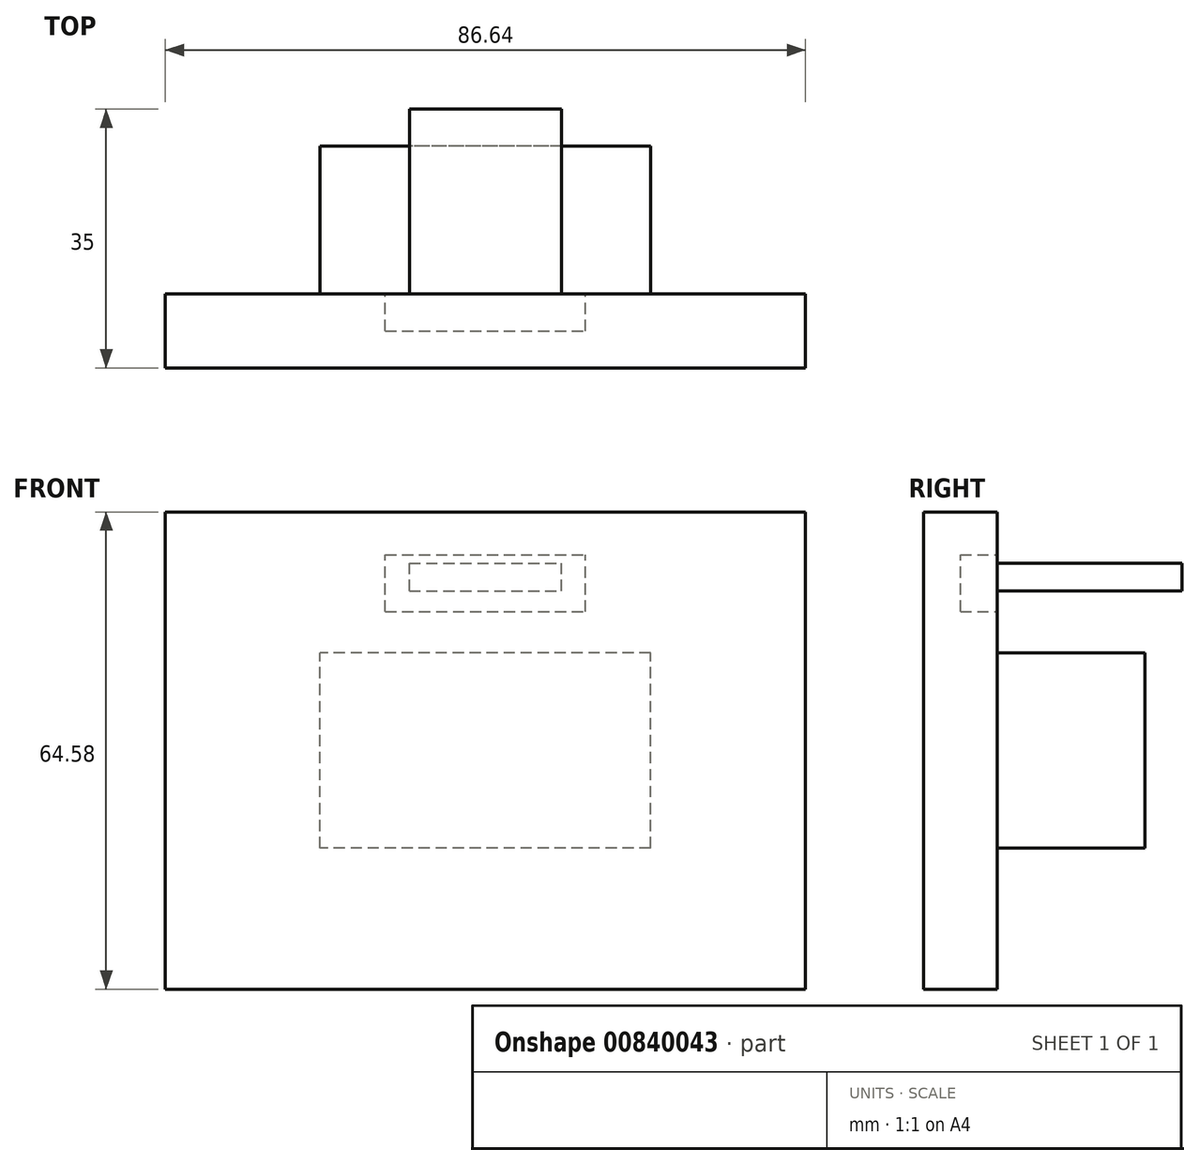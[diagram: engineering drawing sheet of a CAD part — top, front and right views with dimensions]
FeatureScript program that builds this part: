
annotation { "Feature Type Name" : "Feature", "Feature Type Description" : "" }
export const myFeature = defineFeature(function(context is Context, id is Id, definition is map)
    precondition{}
    {
        {
            var Q0;
            Q0=qCreatedBy(makeId("Front.planeOp"),FACE);
            var sketch = newSketch(context, id + "F0", { "sketchPlane" : qUnion([Q0])});
            skLineSegment(sketch, "E0.bottom", {"start": v(43.32, -32.3) * mm, "end": v(-43.32, -32.3) * mm});
            skLineSegment(sketch, "E0.top", {"start": v(43.32, 32.3) * mm, "end": v(-43.32, 32.3) * mm});
            skLineSegment(sketch, "E0.left", {"start": v(43.32, -32.3) * mm, "end": v(43.32, 32.3) * mm});
            skLineSegment(sketch, "E0.right", {"start": v(-43.32, -32.3) * mm, "end": v(-43.32, 32.3) * mm});
            skPoint(sketch, "E0.middle", {"position": v(0, 0) * mm});
            skSolve(sketch);
        }
        {
            var Q0;
            Q0 = qSketchRegion(id + "F0", true);
            extrude(context, id + "F1", {"entities" : qUnion([Q0]), "depth" : 10 * mm, "offsetDistance" : 25 * mm});
        }
        {
            var Q0;
            Q0=makeQuery(id+"F1.opExtrude","CAP_FACE",FACE,{"disambiguationData":[OSD([sQuery(id+"F0.wireOp",EDGE,"E0.bottom"),sQuery(id+"F0.wireOp",EDGE,"E0.top"),sQuery(id+"F0.wireOp",EDGE,"E0.left"),sQuery(id+"F0.wireOp",EDGE,"E0.right")])],"isStart":true});
            var sketch = newSketch(context, id + "F2", { "sketchPlane" : qUnion([Q0])});
            skLineSegment(sketch, "E1.bottom", {"start": v(13.57, 18.8) * mm, "end": v(-13.57, 18.8) * mm});
            skLineSegment(sketch, "E1.top", {"start": v(13.57, 26.46) * mm, "end": v(-13.57, 26.46) * mm});
            skLineSegment(sketch, "E1.left", {"start": v(13.57, 18.8) * mm, "end": v(13.57, 26.46) * mm});
            skLineSegment(sketch, "E1.right", {"start": v(-13.57, 18.8) * mm, "end": v(-13.57, 26.46) * mm});
            skPoint(sketch, "E1.middle", {"position": v(0, 22.63) * mm});
            skSolve(sketch);
        }
        {
            var Q0;
            Q0 = qSketchRegion(id + "F2", true);
            extrude(context, id + "F3", {"entities" : qUnion([Q0]), "operationType" : NewBodyOperationType.REMOVE, "oppositeDirection" : true, "depth" : 5 * mm, "offsetDistance" : 25 * mm});
        }
        {
            var Q0;
            Q0=makeQuery(id+"F1.opExtrude","CAP_FACE",FACE,{"disambiguationData":[OSD([sQuery(id+"F0.wireOp",EDGE,"E0.bottom"),sQuery(id+"F0.wireOp",EDGE,"E0.top"),sQuery(id+"F0.wireOp",EDGE,"E0.left"),sQuery(id+"F0.wireOp",EDGE,"E0.right")])],"isStart":true});
            var sketch = newSketch(context, id + "F4", { "sketchPlane" : qUnion([Q0])});
            skLineSegment(sketch, "E2.bottom", {"start": v(-22.37, -13.2) * mm, "end": v(22.37, -13.2) * mm});
            skLineSegment(sketch, "E2.top", {"start": v(-22.37, 13.2) * mm, "end": v(22.37, 13.2) * mm});
            skLineSegment(sketch, "E2.left", {"start": v(-22.37, -13.2) * mm, "end": v(-22.37, 13.2) * mm});
            skLineSegment(sketch, "E2.right", {"start": v(22.37, -13.2) * mm, "end": v(22.37, 13.2) * mm});
            skPoint(sketch, "E2.middle", {"position": v(0, 0) * mm});
            skSolve(sketch);
        }
        {
            var Q0;
            Q0 = qSketchRegion(id + "F4", true);
            extrude(context, id + "F5", {"entities" : qUnion([Q0]), "operationType" : NewBodyOperationType.ADD, "depth" : 20 * mm, "offsetDistance" : 25 * mm});
        }
        {
            var Q0;
            Q0=makeQuery(id+"F1.opExtrude","CAP_FACE",FACE,{"disambiguationData":[OSD([sQuery(id+"F0.wireOp",EDGE,"E0.bottom"),sQuery(id+"F0.wireOp",EDGE,"E0.top"),sQuery(id+"F0.wireOp",EDGE,"E0.left"),sQuery(id+"F0.wireOp",EDGE,"E0.right")])],"isStart":true});
            var sketch = newSketch(context, id + "F6", { "sketchPlane" : qUnion([Q0])});
            skLineSegment(sketch, "E3.bottom", {"start": v(10.3, 21.6) * mm, "end": v(-10.3, 21.6) * mm});
            skLineSegment(sketch, "E3.top", {"start": v(10.3, 25.35) * mm, "end": v(-10.3, 25.35) * mm});
            skLineSegment(sketch, "E3.left", {"start": v(10.3, 21.6) * mm, "end": v(10.3, 25.35) * mm});
            skLineSegment(sketch, "E3.right", {"start": v(-10.3, 21.6) * mm, "end": v(-10.3, 25.35) * mm});
            skPoint(sketch, "E3.middle", {"position": v(0, 23.47) * mm});
            skSolve(sketch);
        }
        {
            var Q0;
            Q0 = qSketchRegion(id + "F6", true);
            extrude(context, id + "F7", {"entities" : qUnion([Q0]), "depth" : 25 * mm, "offsetDistance" : 25 * mm});
        }
    });
